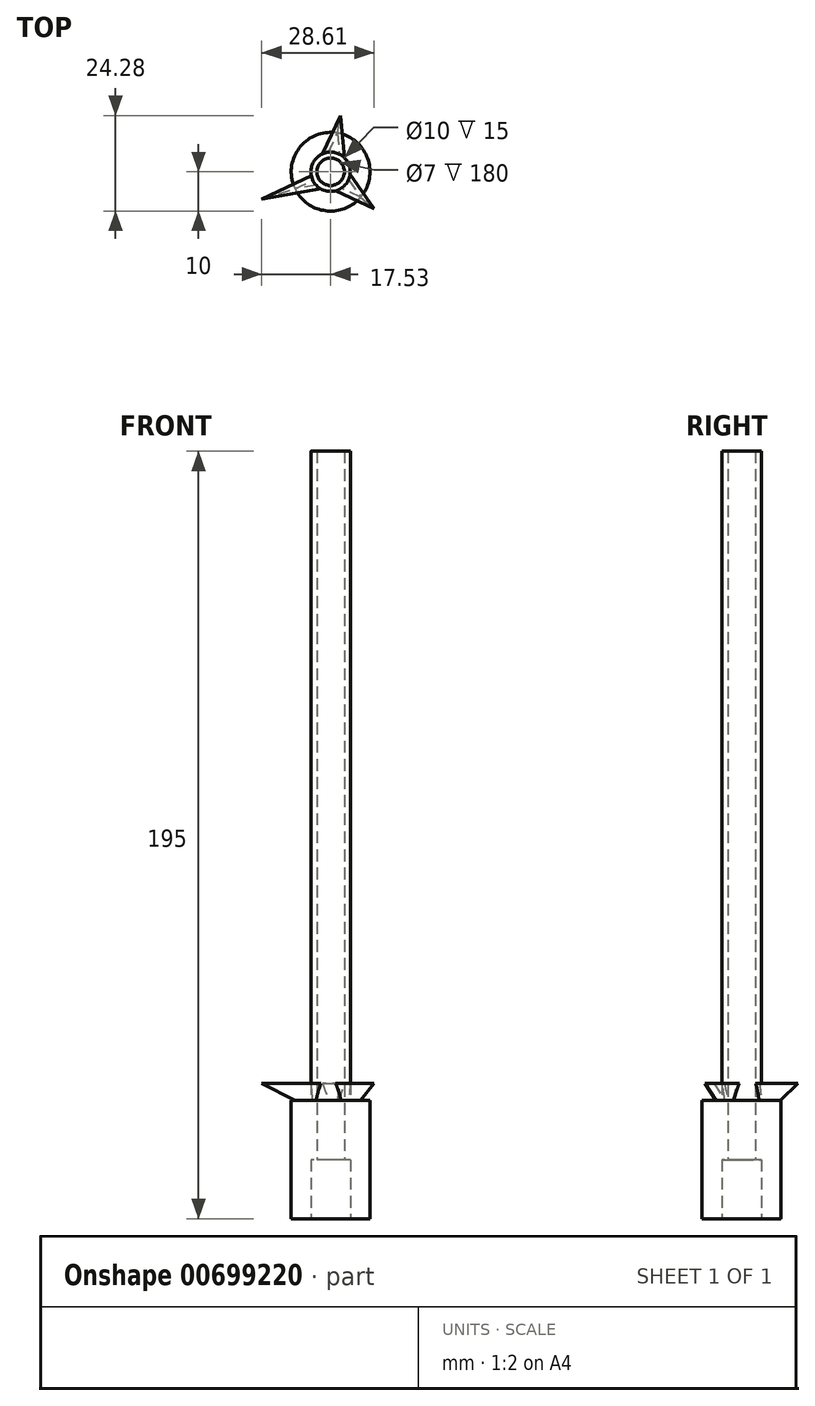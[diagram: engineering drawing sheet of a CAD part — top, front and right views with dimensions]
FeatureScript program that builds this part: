
annotation { "Feature Type Name" : "Feature", "Feature Type Description" : "" }
export const myFeature = defineFeature(function(context is Context, id is Id, definition is map)
    precondition{}
    {
        {
            var Q0;
            Q0=qCreatedBy(makeId("Top.planeOp"),FACE);
            var sketch = newSketch(context, id + "F0", { "sketchPlane" : qUnion([Q0])});
            skCircle(sketch, "E0", {"center": v(0, 0) * mm, "radius": 10 * mm});
            skCircle(sketch, "E1", {"center": v(0, 0) * mm, "radius": 5 * mm});
            skSolve(sketch);
        }
        {
            var Q0;
            Q0=makeQuery(id+"F0.imprint","IMPRINT",FACE,{"disambiguationData":[TD([[makeQuery(id+"F0.imprint","IMPRINT",EDGE,{"derivedFrom":sQuery(id+"F0.wireOp",EDGE,"E0")}),1.0]])]});
            extrude(context, id + "F1", {"entities" : qUnion([Q0]), "endBound" : BoundingType.SYMMETRIC, "depth" : 30 * mm, "offsetDistance" : 25 * mm});
        }
        {
            var Q0;
            Q0=qCreatedBy(makeId("Top.planeOp"),FACE);
            var sketch = newSketch(context, id + "F2", { "sketchPlane" : qUnion([Q0])});
            skCircle(sketch, "E2", {"center": v(0, 0) * mm, "radius": 5 * mm});
            skCircle(sketch, "E3", {"center": v(0, 0) * mm, "radius": 3.5 * mm});
            skSolve(sketch);
        }
        {
            var Q0;
            Q0 = qSketchRegion(id + "F2", true);
            extrude(context, id + "F3", {"entities" : qUnion([Q0]), "operationType" : NewBodyOperationType.ADD, "depth" : 180 * mm, "offsetDistance" : 25 * mm});
        }
        {
            var Q0;
            Q0=makeQuery(id+"F1.opExtrude","CAP_FACE",FACE,{"disambiguationData":[OSD([sQuery(id+"F0.wireOp",EDGE,"E0"),sQuery(id+"F0.wireOp",EDGE,"E1")])],"isStart":false});
            var sketch = newSketch(context, id + "F4", { "sketchPlane" : qUnion([Q0])});
            skLineSegment(sketch, "E4", {"start": v(1.74, 9.85) * mm, "end": v(0.87, 4.92) * mm});
            skLineSegment(sketch, "E5", {"start": v(0.87, 4.92) * mm, "end": v(-0.56, 4.97) * mm});
            skLineSegment(sketch, "E6", {"start": v(-0.56, 4.97) * mm, "end": v(1.74, 9.85) * mm});
            skLineSegment(sketch, "E7.MirrorCS", {"start": v(2.23, 4.48) * mm, "end": v(1.74, 9.85) * mm});
            skLineSegment(sketch, "E8.MirrorCS", {"start": v(0.87, 4.92) * mm, "end": v(2.23, 4.48) * mm});
            skSolve(sketch);
        }
        {
            var Q0;
            {var subQ0=sQuery(id+"F4.wireOp",EDGE,"E4");Q0=makeQuery(id+"F4.imprint","IMPRINT",FACE,{"disambiguationData":[TD([[makeQuery(id+"F4.imprint","IMPRINT",EDGE,{"derivedFrom":subQ0}),-1.0]])]});}
            var Q1;
            {var subQ0=sQuery(id+"F4.wireOp",EDGE,"E4");Q1=makeQuery(id+"F4.imprint","IMPRINT",FACE,{"disambiguationData":[TD([[makeQuery(id+"F4.imprint","IMPRINT",EDGE,{"derivedFrom":subQ0}),1.0]])]});}
            extrude(context, id + "F5", {"entities" : qUnion([Q0, Q1]), "operationType" : NewBodyOperationType.ADD, "depth" : 4.4 * mm, "offsetDistance" : 25 * mm, "hasDraft" : true, "draftAngle" : 15 * degree});
        }
        {
            var Q0;
            Q0=makeQuery(id+"F1.opExtrude","CAP_FACE",FACE,{"disambiguationData":[OSD([sQuery(id+"F0.wireOp",EDGE,"E0"),sQuery(id+"F0.wireOp",EDGE,"E1")])],"isStart":false});
            var sketch = newSketch(context, id + "F6", { "sketchPlane" : qUnion([Q0])});
            skLineSegment(sketch, "E9", {"start": v(-9.02, -4.3) * mm, "end": v(-4.5, -2.18) * mm});
            skLineSegment(sketch, "E10", {"start": v(-4.5, -2.18) * mm, "end": v(-3.7, -3.37) * mm});
            skLineSegment(sketch, "E11", {"start": v(-3.7, -3.37) * mm, "end": v(-9.02, -4.3) * mm});
            skLineSegment(sketch, "E12.MirrorCS", {"start": v(-4.9, -0.81) * mm, "end": v(-9.02, -4.3) * mm});
            skLineSegment(sketch, "E13.MirrorCS", {"start": v(-4.5, -2.18) * mm, "end": v(-4.9, -0.81) * mm});
            skSolve(sketch);
        }
        {
            var Q0;
            {var subQ1=sQuery(id+"F6.wireOp",EDGE,"E9");var subQ3=makeQuery(id+"F1.opExtrude","CAP_EDGE",EDGE,{"disambiguationData":[OSD([sQuery(id+"F0.wireOp",EDGE,"E1")])],"isStart":false});var subQ4=makeQuery(id+"F6.imprint","INTERSECT",VERTEX,{"derivedFrom":[subQ3,subQ1]});Q0=makeQuery(id+"F6.imprint","IMPRINT",FACE,{"disambiguationData":[TD([[makeQuery(id+"F6.imprint","IMPRINT",EDGE,{"disambiguationData":[TD([[subQ4,1.0]])],"derivedFrom":subQ3}),-1.0]])]});}
            var Q1;
            {var subQ0=sQuery(id+"F6.wireOp",EDGE,"E11");Q1=makeQuery(id+"F6.imprint","IMPRINT",FACE,{"disambiguationData":[TD([[makeQuery(id+"F6.imprint","IMPRINT",EDGE,{"derivedFrom":subQ0}),-1.0]])]});}
            extrude(context, id + "F7", {"entities" : qUnion([Q0, Q1]), "operationType" : NewBodyOperationType.ADD, "depth" : 4.4 * mm, "offsetDistance" : 25 * mm, "hasDraft" : true, "draftAngle" : 15 * degree});
        }
        {
            var Q0;
            Q0=makeQuery(id+"F1.opExtrude","CAP_FACE",FACE,{"disambiguationData":[OSD([sQuery(id+"F0.wireOp",EDGE,"E0"),sQuery(id+"F0.wireOp",EDGE,"E1")])],"isStart":false});
            var sketch = newSketch(context, id + "F8", { "sketchPlane" : qUnion([Q0])});
            skLineSegment(sketch, "E14", {"start": v(7.64, -6.47) * mm, "end": v(3.81, -3.26) * mm});
            skLineSegment(sketch, "E15", {"start": v(3.81, -3.26) * mm, "end": v(4.56, -2.04) * mm});
            skLineSegment(sketch, "E16", {"start": v(4.56, -2.04) * mm, "end": v(7.64, -6.47) * mm});
            skLineSegment(sketch, "E17.MirrorCS", {"start": v(2.75, -4.2) * mm, "end": v(7.64, -6.47) * mm});
            skLineSegment(sketch, "E18.MirrorCS", {"start": v(3.81, -3.26) * mm, "end": v(2.75, -4.2) * mm});
            skSolve(sketch);
        }
        {
            var Q0;
            Q0 = qSketchRegion(id + "F8", true);
            extrude(context, id + "F9", {"entities" : qUnion([Q0]), "operationType" : NewBodyOperationType.ADD, "depth" : 4.4 * mm, "offsetDistance" : 25 * mm, "hasDraft" : true, "draftAngle" : 15 * degree});
        }
    });
